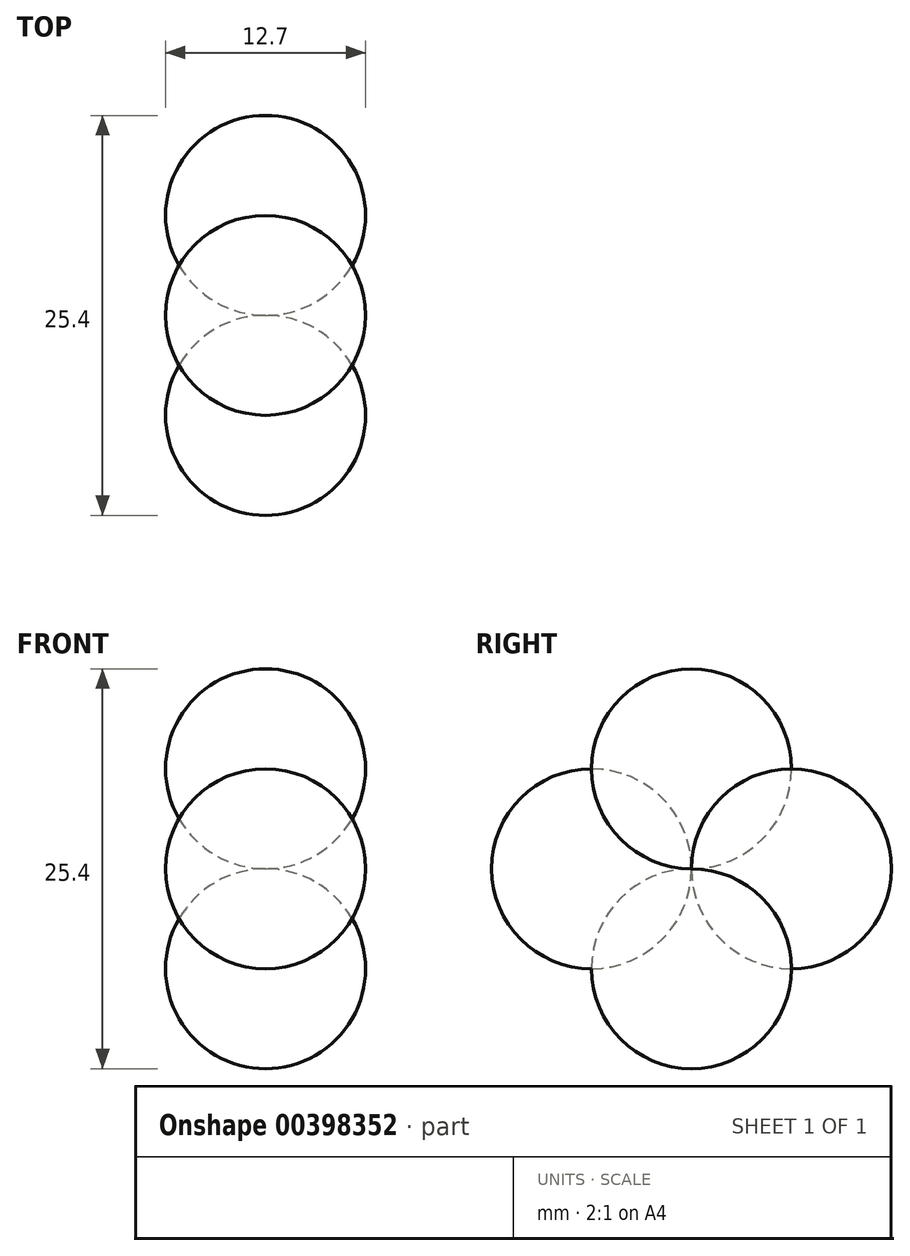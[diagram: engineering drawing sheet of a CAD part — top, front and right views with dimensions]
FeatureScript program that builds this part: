
annotation { "Feature Type Name" : "Feature", "Feature Type Description" : "" }
export const myFeature = defineFeature(function(context is Context, id is Id, definition is map)
    precondition{}
    {
        {
            var Q0;
            Q0=qCreatedBy(makeId("Right.planeOp"),FACE);
            var sketch = newSketch(context, id + "F0", { "sketchPlane" : qUnion([Q0])});
            skLineSegment(sketch, "E0", {"start": v(0, 0) * mm, "end": v(0, -12.7) * mm});
            skArc(sketch, "E1", {"start": v(0, -12.7) * mm, "mid": v(6.35, -6.35) * mm, "end": v(0, 0) * mm});
            skSolve(sketch);
        }
        {
            var Q0;
            Q0 = qSketchRegion(id + "F0", true);
            var Q1;
            Q1=sQuery(id+"F0.wireOp",EDGE,"E0");
            revolve(context, id + "F1", {"entities" : qUnion([Q0]), "axis" : qUnion([Q1]), "revolveType" : RevolveType.FULL});
        }
        {
            var Q0;
            Q0=qCreatedBy(makeId("Right.planeOp"),FACE);
            var sketch = newSketch(context, id + "F2", { "sketchPlane" : qUnion([Q0])});
            skLineSegment(sketch, "E2", {"start": v(0, 0) * mm, "end": v(0, 12.7) * mm});
            skArc(sketch, "E3", {"start": v(0, 0) * mm, "mid": v(6.35, 6.35) * mm, "end": v(0, 12.7) * mm});
            skSolve(sketch);
        }
        {
            var Q0;
            Q0=makeQuery(id+"F2.imprint","IMPRINT",FACE,{"disambiguationData":[TD([[makeQuery(id+"F2.imprint","IMPRINT",EDGE,{"derivedFrom":sQuery(id+"F2.wireOp",EDGE,"E2")}),-1.0]])]});
            var Q1;
            Q1=sQuery(id+"F2.wireOp",EDGE,"E2");
            revolve(context, id + "F3", {"entities" : qUnion([Q0]), "axis" : qUnion([Q1]), "revolveType" : RevolveType.FULL});
        }
        {
            var Q0;
            Q0=qCreatedBy(makeId("Right.planeOp"),FACE);
            var sketch = newSketch(context, id + "F4", { "sketchPlane" : qUnion([Q0])});
            skLineSegment(sketch, "E4", {"start": v(0, 0) * mm, "end": v(-12.7, 0) * mm});
            skLineSegment(sketch, "E5", {"start": v(0, 0) * mm, "end": v(12.7, 0) * mm});
            skArc(sketch, "E6", {"start": v(0, 0) * mm, "mid": v(6.35, -6.35) * mm, "end": v(12.7, 0) * mm});
            skSolve(sketch);
        }
        {
            var Q0;
            Q0=makeQuery(id+"F4.imprint","IMPRINT",FACE,{"disambiguationData":[TD([[makeQuery(id+"F4.imprint","IMPRINT",EDGE,{"derivedFrom":sQuery(id+"F4.wireOp",EDGE,"E5")}),-1.0]])]});
            var Q1;
            Q1=sQuery(id+"F4.wireOp",EDGE,"E5");
            revolve(context, id + "F5", {"entities" : qUnion([Q0]), "axis" : qUnion([Q1]), "revolveType" : RevolveType.FULL});
        }
        {
            var Q0;
            Q0=qCreatedBy(makeId("Right.planeOp"),FACE);
            var sketch = newSketch(context, id + "F6", { "sketchPlane" : qUnion([Q0])});
            skLineSegment(sketch, "E7", {"start": v(0, 0) * mm, "end": v(-12.7, 0) * mm});
            skArc(sketch, "E8", {"start": v(0, 0) * mm, "mid": v(-6.35, 6.35) * mm, "end": v(-12.7, 0) * mm});
            skSolve(sketch);
        }
        {
            var Q0;
            Q0=makeQuery(id+"F6.imprint","IMPRINT",FACE,{"disambiguationData":[TD([[makeQuery(id+"F6.imprint","IMPRINT",EDGE,{"derivedFrom":sQuery(id+"F6.wireOp",EDGE,"E7")}),-1.0]])]});
            var Q1;
            Q1=sQuery(id+"F6.wireOp",EDGE,"E7");
            revolve(context, id + "F7", {"entities" : qUnion([Q0]), "axis" : qUnion([Q1]), "revolveType" : RevolveType.FULL});
        }
    });
